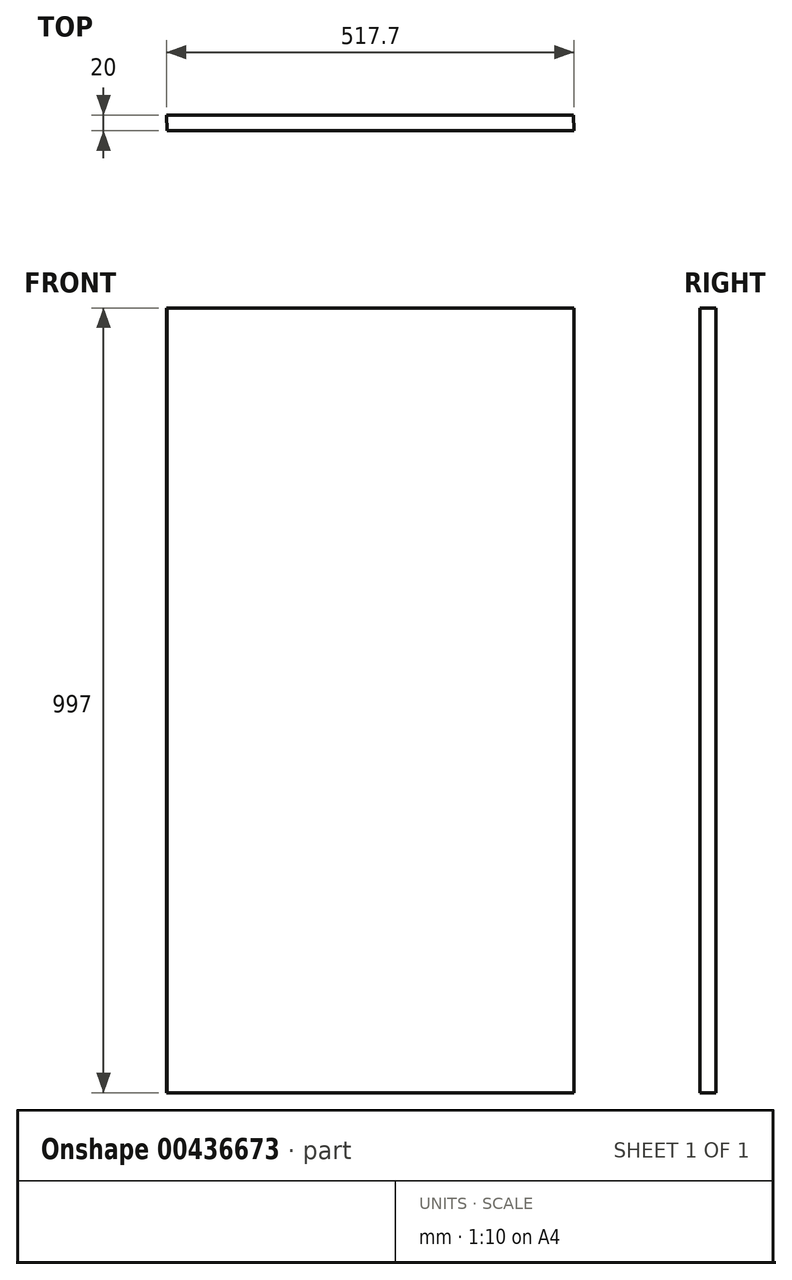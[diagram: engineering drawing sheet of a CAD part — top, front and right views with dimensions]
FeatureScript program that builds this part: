
annotation { "Feature Type Name" : "Feature", "Feature Type Description" : "" }
export const myFeature = defineFeature(function(context is Context, id is Id, definition is map)
    precondition{}
    {
        {
            var Q0;
            Q0=qCreatedBy(makeId("Top.planeOp"),FACE);
            var sketch = newSketch(context, id + "F0", { "sketchPlane" : qUnion([Q0])});
            skLineSegment(sketch, "E0.bottom", {"start": v(267.76, 85.72) * mm, "end": v(-249.24, 85.72) * mm});
            skLineSegment(sketch, "E0.top", {"start": v(267.06, 105.72) * mm, "end": v(-249.94, 105.72) * mm});
            skPoint(sketch, "E0.middle", {"position": v(0, 0) * mm});
            skLineSegment(sketch, "E1", {"start": v(-249.94, 105.72) * mm, "end": v(-249.24, 85.72) * mm});
            skLineSegment(sketch, "E2", {"start": v(267.06, 105.72) * mm, "end": v(267.76, 85.72) * mm});
            skSolve(sketch);
        }
        {
            var Q0;
            Q0 = qSketchRegion(id + "F0", true);
            extrude(context, id + "F1", {"entities" : qUnion([Q0]), "depth" : 997 * mm});
        }
    });
